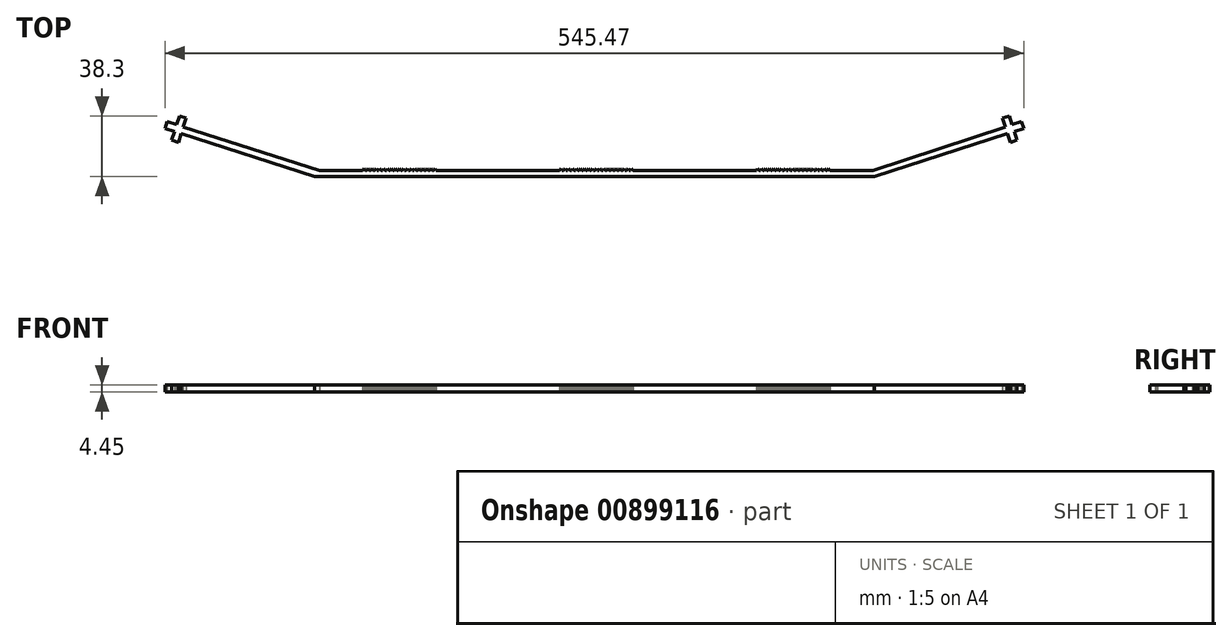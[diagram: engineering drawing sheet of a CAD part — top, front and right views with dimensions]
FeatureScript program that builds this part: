
annotation { "Feature Type Name" : "Feature", "Feature Type Description" : "" }
export const myFeature = defineFeature(function(context is Context, id is Id, definition is map)
    precondition{}
    {
        {
            var Q0;
            Q0=qCreatedBy(makeId("Top.planeOp"),FACE);
            var sketch = newSketch(context, id + "F0", { "sketchPlane" : qUnion([Q0])});
            skLineSegment(sketch, "E0", {"start": v(-248.6, 5.73) * mm, "end": v(107, 5.73) * mm});
            skLineSegment(sketch, "E1", {"start": v(-248.6, 5.73) * mm, "end": v(-333.25, 32.88) * mm});
            skLineSegment(sketch, "E2", {"start": v(-333.25, 32.88) * mm, "end": v(-335.04, 27.33) * mm});
            skLineSegment(sketch, "E3", {"start": v(-335.04, 27.33) * mm, "end": v(-339.27, 28.69) * mm});
            skLineSegment(sketch, "E4", {"start": v(-339.27, 28.69) * mm, "end": v(-337.5, 34.24) * mm});
            skLineSegment(sketch, "E5", {"start": v(-337.5, 34.24) * mm, "end": v(-343.54, 36.18) * mm});
            skLineSegment(sketch, "E6", {"start": v(-343.54, 36.18) * mm, "end": v(-342.18, 40.42) * mm});
            skLineSegment(sketch, "E7", {"start": v(-342.18, 40.42) * mm, "end": v(-336.13, 38.48) * mm});
            skLineSegment(sketch, "E8", {"start": v(-336.13, 38.48) * mm, "end": v(-334.35, 44.03) * mm});
            skLineSegment(sketch, "E9", {"start": v(-334.35, 44.03) * mm, "end": v(-330.11, 42.67) * mm});
            skLineSegment(sketch, "E10", {"start": v(-330.11, 42.67) * mm, "end": v(-331.9, 37.12) * mm});
            skLineSegment(sketch, "E11", {"start": v(-331.9, 37.12) * mm, "end": v(-247.24, 9.97) * mm});
            skLineSegment(sketch, "E12", {"start": v(-245.43, 9.39) * mm, "end": v(-217.94, 9.39) * mm});
            skLineSegment(sketch, "E13", {"start": v(-69.57, 10.53) * mm, "end": v(-68.7, 9.39) * mm});
            skLineSegment(sketch, "E14.MirrorCS", {"start": v(-69.57, 10.53) * mm, "end": v(-70.44, 9.39) * mm});
            skLineSegment(sketch, "E15.trimOffspring", {"start": v(-68.7, 9.39) * mm, "end": v(-67.94, 9.39) * mm});
            skPoint(sketch, "E16.start.orphan", {"position": v(-69.57, 3.34) * mm});
            skLineSegment(sketch, "E17.direction1", {"start": v(-68.7, 9.39) * mm, "end": v(-67.94, 9.39) * mm, "construction": true});
            skLineSegment(sketch, "E18.1.0.0", {"start": v(-67.07, 10.53) * mm, "end": v(-66.2, 9.39) * mm});
            skLineSegment(sketch, "E18.1.0.1", {"start": v(-67.07, 10.53) * mm, "end": v(-67.94, 9.39) * mm});
            skLineSegment(sketch, "E18.2.0.0", {"start": v(-64.57, 10.53) * mm, "end": v(-63.7, 9.39) * mm});
            skLineSegment(sketch, "E18.2.0.1", {"start": v(-64.57, 10.53) * mm, "end": v(-65.44, 9.39) * mm});
            skLineSegment(sketch, "E18.3.0.0", {"start": v(-62.07, 10.53) * mm, "end": v(-61.2, 9.39) * mm});
            skLineSegment(sketch, "E18.3.0.1", {"start": v(-62.07, 10.53) * mm, "end": v(-62.94, 9.39) * mm});
            skLineSegment(sketch, "E18.4.0.0", {"start": v(-59.57, 10.53) * mm, "end": v(-58.7, 9.39) * mm});
            skLineSegment(sketch, "E18.4.0.1", {"start": v(-59.57, 10.53) * mm, "end": v(-60.44, 9.39) * mm});
            skLineSegment(sketch, "E18.5.0.0", {"start": v(-57.07, 10.53) * mm, "end": v(-56.2, 9.39) * mm});
            skLineSegment(sketch, "E18.5.0.1", {"start": v(-57.07, 10.53) * mm, "end": v(-57.94, 9.39) * mm});
            skLineSegment(sketch, "E18.6.0.0", {"start": v(-54.57, 10.53) * mm, "end": v(-53.7, 9.39) * mm});
            skLineSegment(sketch, "E18.6.0.1", {"start": v(-54.57, 10.53) * mm, "end": v(-55.44, 9.39) * mm});
            skLineSegment(sketch, "E18.7.0.0", {"start": v(-52.07, 10.53) * mm, "end": v(-51.2, 9.39) * mm});
            skLineSegment(sketch, "E18.7.0.1", {"start": v(-52.07, 10.53) * mm, "end": v(-52.94, 9.39) * mm});
            skLineSegment(sketch, "E18.8.0.0", {"start": v(-49.57, 10.53) * mm, "end": v(-48.7, 9.39) * mm});
            skLineSegment(sketch, "E18.8.0.1", {"start": v(-49.57, 10.53) * mm, "end": v(-50.44, 9.39) * mm});
            skLineSegment(sketch, "E18.9.0.0", {"start": v(-47.07, 10.53) * mm, "end": v(-46.2, 9.39) * mm});
            skLineSegment(sketch, "E18.9.0.1", {"start": v(-47.07, 10.53) * mm, "end": v(-47.94, 9.39) * mm});
            skLineSegment(sketch, "E19.1.0.0", {"start": v(-72.07, 10.53) * mm, "end": v(-72.94, 9.39) * mm});
            skLineSegment(sketch, "E19.1.0.1", {"start": v(-72.07, 10.53) * mm, "end": v(-71.2, 9.39) * mm});
            skLineSegment(sketch, "E19.2.0.0", {"start": v(-74.57, 10.53) * mm, "end": v(-75.44, 9.39) * mm});
            skLineSegment(sketch, "E19.2.0.1", {"start": v(-74.57, 10.53) * mm, "end": v(-73.7, 9.39) * mm});
            skLineSegment(sketch, "E19.3.0.0", {"start": v(-77.07, 10.53) * mm, "end": v(-77.94, 9.39) * mm});
            skLineSegment(sketch, "E19.3.0.1", {"start": v(-77.07, 10.53) * mm, "end": v(-76.2, 9.39) * mm});
            skLineSegment(sketch, "E19.4.0.0", {"start": v(-79.57, 10.53) * mm, "end": v(-80.44, 9.39) * mm});
            skLineSegment(sketch, "E19.4.0.1", {"start": v(-79.57, 10.53) * mm, "end": v(-78.7, 9.39) * mm});
            skLineSegment(sketch, "E19.5.0.0", {"start": v(-82.07, 10.53) * mm, "end": v(-82.94, 9.39) * mm});
            skLineSegment(sketch, "E19.5.0.1", {"start": v(-82.07, 10.53) * mm, "end": v(-81.2, 9.39) * mm});
            skLineSegment(sketch, "E19.6.0.0", {"start": v(-84.57, 10.53) * mm, "end": v(-85.44, 9.39) * mm});
            skLineSegment(sketch, "E19.6.0.1", {"start": v(-84.57, 10.53) * mm, "end": v(-83.7, 9.39) * mm});
            skLineSegment(sketch, "E19.7.0.0", {"start": v(-87.07, 10.53) * mm, "end": v(-87.94, 9.39) * mm});
            skLineSegment(sketch, "E19.7.0.1", {"start": v(-87.07, 10.53) * mm, "end": v(-86.2, 9.39) * mm});
            skLineSegment(sketch, "E19.8.0.0", {"start": v(-89.57, 10.53) * mm, "end": v(-90.44, 9.39) * mm});
            skLineSegment(sketch, "E19.8.0.1", {"start": v(-89.57, 10.53) * mm, "end": v(-88.7, 9.39) * mm});
            skLineSegment(sketch, "E19.9.0.0", {"start": v(-92.07, 10.53) * mm, "end": v(-92.94, 9.39) * mm});
            skLineSegment(sketch, "E19.9.0.1", {"start": v(-92.07, 10.53) * mm, "end": v(-91.2, 9.39) * mm});
            skLineSegment(sketch, "E19.direction1", {"start": v(-70.44, 9.39) * mm, "end": v(-71.2, 9.39) * mm, "construction": true});
            skLineSegment(sketch, "E20.trimOffspring", {"start": v(-91.2, 9.39) * mm, "end": v(-90.44, 9.39) * mm});
            skLineSegment(sketch, "E21.trimOffspring", {"start": v(-88.7, 9.39) * mm, "end": v(-87.94, 9.39) * mm});
            skLineSegment(sketch, "E22.trimOffspring", {"start": v(-86.2, 9.39) * mm, "end": v(-85.44, 9.39) * mm});
            skLineSegment(sketch, "E23.trimOffspring", {"start": v(-81.2, 9.39) * mm, "end": v(-80.44, 9.39) * mm});
            skLineSegment(sketch, "E24.trimOffspring", {"start": v(-83.7, 9.39) * mm, "end": v(-82.94, 9.39) * mm});
            skLineSegment(sketch, "E25.trimOffspring", {"start": v(-78.7, 9.39) * mm, "end": v(-77.94, 9.39) * mm});
            skLineSegment(sketch, "E26.trimOffspring", {"start": v(-76.2, 9.39) * mm, "end": v(-75.44, 9.39) * mm});
            skLineSegment(sketch, "E27.trimOffspring", {"start": v(-73.7, 9.39) * mm, "end": v(-72.94, 9.39) * mm});
            skLineSegment(sketch, "E28.trimOffspring", {"start": v(-71.2, 9.39) * mm, "end": v(-70.44, 9.39) * mm});
            skLineSegment(sketch, "E29.trimOffspring", {"start": v(-66.2, 9.39) * mm, "end": v(-65.44, 9.39) * mm, "construction": true});
            skLineSegment(sketch, "E30.trimOffspring", {"start": v(-66.2, 9.39) * mm, "end": v(-65.44, 9.39) * mm});
            skLineSegment(sketch, "E31.trimOffspring", {"start": v(-63.7, 9.39) * mm, "end": v(-62.94, 9.39) * mm, "construction": true});
            skLineSegment(sketch, "E32.trimOffspring", {"start": v(-63.7, 9.39) * mm, "end": v(-62.94, 9.39) * mm});
            skLineSegment(sketch, "E33.trimOffspring", {"start": v(-61.2, 9.39) * mm, "end": v(-60.44, 9.39) * mm, "construction": true});
            skLineSegment(sketch, "E34.trimOffspring", {"start": v(-58.7, 9.39) * mm, "end": v(-57.94, 9.39) * mm, "construction": true});
            skLineSegment(sketch, "E35.trimOffspring", {"start": v(-58.7, 9.39) * mm, "end": v(-57.94, 9.39) * mm});
            skLineSegment(sketch, "E36", {"start": v(-61.2, 9.39) * mm, "end": v(-60.44, 9.39) * mm});
            skLineSegment(sketch, "E37.trimOffspring", {"start": v(-56.2, 9.39) * mm, "end": v(-55.44, 9.39) * mm, "construction": true});
            skLineSegment(sketch, "E38.trimOffspring", {"start": v(-56.2, 9.39) * mm, "end": v(-55.44, 9.39) * mm});
            skLineSegment(sketch, "E39.trimOffspring", {"start": v(-53.7, 9.39) * mm, "end": v(-52.94, 9.39) * mm, "construction": true});
            skLineSegment(sketch, "E40.trimOffspring", {"start": v(-53.7, 9.39) * mm, "end": v(-52.94, 9.39) * mm});
            skLineSegment(sketch, "E41.trimOffspring", {"start": v(-51.2, 9.39) * mm, "end": v(-50.44, 9.39) * mm, "construction": true});
            skLineSegment(sketch, "E42.trimOffspring", {"start": v(-51.2, 9.39) * mm, "end": v(-50.44, 9.39) * mm});
            skLineSegment(sketch, "E43.trimOffspring", {"start": v(-48.7, 9.39) * mm, "end": v(-47.94, 9.39) * mm, "construction": true});
            skLineSegment(sketch, "E44.trimOffspring", {"start": v(-48.7, 9.39) * mm, "end": v(-47.94, 9.39) * mm});
            skLineSegment(sketch, "E45.trimOffspring", {"start": v(-46.2, 9.39) * mm, "end": v(-43.7, 9.39) * mm, "construction": true});
            skLineSegment(sketch, "E46.trimOffspring", {"start": v(-46.2, 9.39) * mm, "end": v(32.06, 9.39) * mm});
            skLineSegment(sketch, "E47.1.0.0", {"start": v(77.93, 10.53) * mm, "end": v(78.8, 9.39) * mm});
            skLineSegment(sketch, "E47.1.0.1", {"start": v(77.93, 10.53) * mm, "end": v(77.06, 9.39) * mm});
            skLineSegment(sketch, "E47.1.0.2", {"start": v(75.43, 10.53) * mm, "end": v(76.3, 9.39) * mm});
            skLineSegment(sketch, "E47.1.0.3", {"start": v(75.43, 10.53) * mm, "end": v(74.56, 9.39) * mm});
            skLineSegment(sketch, "E47.1.0.4", {"start": v(72.93, 10.53) * mm, "end": v(73.8, 9.39) * mm});
            skLineSegment(sketch, "E47.1.0.5", {"start": v(72.93, 10.53) * mm, "end": v(72.06, 9.39) * mm});
            skLineSegment(sketch, "E47.1.0.6", {"start": v(70.43, 10.53) * mm, "end": v(71.3, 9.39) * mm});
            skLineSegment(sketch, "E47.1.0.7", {"start": v(70.43, 10.53) * mm, "end": v(69.56, 9.39) * mm});
            skLineSegment(sketch, "E47.1.0.8", {"start": v(67.93, 10.53) * mm, "end": v(68.8, 9.39) * mm});
            skLineSegment(sketch, "E47.1.0.9", {"start": v(67.93, 10.53) * mm, "end": v(67.06, 9.39) * mm});
            skLineSegment(sketch, "E47.1.0.10", {"start": v(65.43, 10.53) * mm, "end": v(66.3, 9.39) * mm});
            skLineSegment(sketch, "E47.1.0.11", {"start": v(65.43, 10.53) * mm, "end": v(64.56, 9.39) * mm});
            skLineSegment(sketch, "E47.1.0.12", {"start": v(62.93, 10.53) * mm, "end": v(63.8, 9.39) * mm});
            skLineSegment(sketch, "E47.1.0.13", {"start": v(62.93, 10.53) * mm, "end": v(62.06, 9.39) * mm});
            skLineSegment(sketch, "E47.1.0.14", {"start": v(60.43, 10.53) * mm, "end": v(61.3, 9.39) * mm});
            skLineSegment(sketch, "E47.1.0.15", {"start": v(60.43, 10.53) * mm, "end": v(59.56, 9.39) * mm});
            skLineSegment(sketch, "E47.1.0.16", {"start": v(57.93, 10.53) * mm, "end": v(58.8, 9.39) * mm});
            skLineSegment(sketch, "E47.1.0.17", {"start": v(57.93, 10.53) * mm, "end": v(57.06, 9.39) * mm});
            skLineSegment(sketch, "E47.1.0.18", {"start": v(55.43, 10.53) * mm, "end": v(56.3, 9.39) * mm});
            skLineSegment(sketch, "E47.1.0.19", {"start": v(55.43, 10.53) * mm, "end": v(54.56, 9.39) * mm});
            skLineSegment(sketch, "E47.1.0.20", {"start": v(52.93, 10.53) * mm, "end": v(53.8, 9.39) * mm});
            skLineSegment(sketch, "E47.1.0.21", {"start": v(52.93, 10.53) * mm, "end": v(52.06, 9.39) * mm});
            skLineSegment(sketch, "E47.1.0.22", {"start": v(50.43, 10.53) * mm, "end": v(51.3, 9.39) * mm});
            skLineSegment(sketch, "E47.1.0.23", {"start": v(50.43, 10.53) * mm, "end": v(49.56, 9.39) * mm});
            skLineSegment(sketch, "E47.1.0.24", {"start": v(47.93, 10.53) * mm, "end": v(48.8, 9.39) * mm});
            skLineSegment(sketch, "E47.1.0.25", {"start": v(47.93, 10.53) * mm, "end": v(47.06, 9.39) * mm});
            skLineSegment(sketch, "E47.1.0.26", {"start": v(45.43, 10.53) * mm, "end": v(46.3, 9.39) * mm});
            skLineSegment(sketch, "E47.1.0.27", {"start": v(45.43, 10.53) * mm, "end": v(44.56, 9.39) * mm});
            skLineSegment(sketch, "E47.1.0.28", {"start": v(42.93, 10.53) * mm, "end": v(43.8, 9.39) * mm});
            skLineSegment(sketch, "E47.1.0.29", {"start": v(42.93, 10.53) * mm, "end": v(42.06, 9.39) * mm});
            skLineSegment(sketch, "E47.1.0.30", {"start": v(40.43, 10.53) * mm, "end": v(41.3, 9.39) * mm});
            skLineSegment(sketch, "E47.1.0.31", {"start": v(40.43, 10.53) * mm, "end": v(39.56, 9.39) * mm});
            skLineSegment(sketch, "E47.1.0.32", {"start": v(37.93, 10.53) * mm, "end": v(38.8, 9.39) * mm});
            skLineSegment(sketch, "E47.1.0.33", {"start": v(37.93, 10.53) * mm, "end": v(37.06, 9.39) * mm});
            skLineSegment(sketch, "E47.1.0.34", {"start": v(35.43, 10.53) * mm, "end": v(36.3, 9.39) * mm});
            skLineSegment(sketch, "E47.1.0.35", {"start": v(35.43, 10.53) * mm, "end": v(34.56, 9.39) * mm});
            skLineSegment(sketch, "E47.1.0.36", {"start": v(32.93, 10.53) * mm, "end": v(33.8, 9.39) * mm});
            skLineSegment(sketch, "E47.1.0.37", {"start": v(32.93, 10.53) * mm, "end": v(32.06, 9.39) * mm});
            skLineSegment(sketch, "E48.1.0.0", {"start": v(-172.07, 10.53) * mm, "end": v(-171.2, 9.39) * mm});
            skLineSegment(sketch, "E48.1.0.1", {"start": v(-172.07, 10.53) * mm, "end": v(-172.94, 9.39) * mm});
            skLineSegment(sketch, "E48.1.0.2", {"start": v(-174.57, 10.53) * mm, "end": v(-173.7, 9.39) * mm});
            skLineSegment(sketch, "E48.1.0.3", {"start": v(-174.57, 10.53) * mm, "end": v(-175.44, 9.39) * mm});
            skLineSegment(sketch, "E48.1.0.4", {"start": v(-177.07, 10.53) * mm, "end": v(-176.2, 9.39) * mm});
            skLineSegment(sketch, "E48.1.0.5", {"start": v(-177.07, 10.53) * mm, "end": v(-177.94, 9.39) * mm});
            skLineSegment(sketch, "E48.1.0.6", {"start": v(-179.57, 10.53) * mm, "end": v(-178.7, 9.39) * mm});
            skLineSegment(sketch, "E48.1.0.7", {"start": v(-179.57, 10.53) * mm, "end": v(-180.44, 9.39) * mm});
            skLineSegment(sketch, "E48.1.0.8", {"start": v(-182.07, 10.53) * mm, "end": v(-181.2, 9.39) * mm});
            skLineSegment(sketch, "E48.1.0.9", {"start": v(-182.07, 10.53) * mm, "end": v(-182.94, 9.39) * mm});
            skLineSegment(sketch, "E48.1.0.10", {"start": v(-184.57, 10.53) * mm, "end": v(-183.7, 9.39) * mm});
            skLineSegment(sketch, "E48.1.0.11", {"start": v(-184.57, 10.53) * mm, "end": v(-185.44, 9.39) * mm});
            skLineSegment(sketch, "E48.1.0.12", {"start": v(-187.07, 10.53) * mm, "end": v(-186.2, 9.39) * mm});
            skLineSegment(sketch, "E48.1.0.13", {"start": v(-187.07, 10.53) * mm, "end": v(-187.94, 9.39) * mm});
            skLineSegment(sketch, "E48.1.0.14", {"start": v(-189.57, 10.53) * mm, "end": v(-188.7, 9.39) * mm});
            skLineSegment(sketch, "E48.1.0.15", {"start": v(-189.57, 10.53) * mm, "end": v(-190.44, 9.39) * mm});
            skLineSegment(sketch, "E48.1.0.16", {"start": v(-192.07, 10.53) * mm, "end": v(-191.2, 9.39) * mm});
            skLineSegment(sketch, "E48.1.0.17", {"start": v(-192.07, 10.53) * mm, "end": v(-192.94, 9.39) * mm});
            skLineSegment(sketch, "E48.1.0.18", {"start": v(-194.57, 10.53) * mm, "end": v(-193.7, 9.39) * mm});
            skLineSegment(sketch, "E48.1.0.19", {"start": v(-194.57, 10.53) * mm, "end": v(-195.44, 9.39) * mm});
            skLineSegment(sketch, "E48.1.0.20", {"start": v(-217.07, 10.53) * mm, "end": v(-217.94, 9.39) * mm});
            skLineSegment(sketch, "E48.1.0.21", {"start": v(-217.07, 10.53) * mm, "end": v(-216.2, 9.39) * mm});
            skLineSegment(sketch, "E48.1.0.22", {"start": v(-214.57, 10.53) * mm, "end": v(-215.44, 9.39) * mm});
            skLineSegment(sketch, "E48.1.0.23", {"start": v(-214.57, 10.53) * mm, "end": v(-213.7, 9.39) * mm});
            skLineSegment(sketch, "E48.1.0.24", {"start": v(-212.07, 10.53) * mm, "end": v(-212.94, 9.39) * mm});
            skLineSegment(sketch, "E48.1.0.25", {"start": v(-212.07, 10.53) * mm, "end": v(-211.2, 9.39) * mm});
            skLineSegment(sketch, "E48.1.0.26", {"start": v(-209.57, 10.53) * mm, "end": v(-210.44, 9.39) * mm});
            skLineSegment(sketch, "E48.1.0.27", {"start": v(-209.57, 10.53) * mm, "end": v(-208.7, 9.39) * mm});
            skLineSegment(sketch, "E48.1.0.28", {"start": v(-207.07, 10.53) * mm, "end": v(-207.94, 9.39) * mm});
            skLineSegment(sketch, "E48.1.0.29", {"start": v(-207.07, 10.53) * mm, "end": v(-206.2, 9.39) * mm});
            skLineSegment(sketch, "E48.1.0.30", {"start": v(-204.57, 10.53) * mm, "end": v(-205.44, 9.39) * mm});
            skLineSegment(sketch, "E48.1.0.31", {"start": v(-204.57, 10.53) * mm, "end": v(-203.7, 9.39) * mm});
            skLineSegment(sketch, "E48.1.0.32", {"start": v(-202.07, 10.53) * mm, "end": v(-202.94, 9.39) * mm});
            skLineSegment(sketch, "E48.1.0.33", {"start": v(-202.07, 10.53) * mm, "end": v(-201.2, 9.39) * mm});
            skLineSegment(sketch, "E48.1.0.34", {"start": v(-199.57, 10.53) * mm, "end": v(-200.44, 9.39) * mm});
            skLineSegment(sketch, "E48.1.0.35", {"start": v(-199.57, 10.53) * mm, "end": v(-198.7, 9.39) * mm});
            skLineSegment(sketch, "E48.1.0.36", {"start": v(-197.07, 10.53) * mm, "end": v(-197.94, 9.39) * mm});
            skLineSegment(sketch, "E48.1.0.37", {"start": v(-197.07, 10.53) * mm, "end": v(-196.2, 9.39) * mm});
            skLineSegment(sketch, "E48.direction1", {"start": v(-46.2, 9.39) * mm, "end": v(-171.2, 9.39) * mm, "construction": true});
            skLineSegment(sketch, "E49.trimOffspring", {"start": v(-216.2, 9.39) * mm, "end": v(-215.44, 9.39) * mm});
            skLineSegment(sketch, "E50.trimOffspring", {"start": v(-213.7, 9.39) * mm, "end": v(-212.94, 9.39) * mm});
            skLineSegment(sketch, "E51.trimOffspring", {"start": v(-211.2, 9.39) * mm, "end": v(-210.44, 9.39) * mm});
            skLineSegment(sketch, "E52.trimOffspring", {"start": v(-208.7, 9.39) * mm, "end": v(-207.94, 9.39) * mm});
            skLineSegment(sketch, "E53.trimOffspring", {"start": v(-206.2, 9.39) * mm, "end": v(-205.44, 9.39) * mm});
            skLineSegment(sketch, "E54.trimOffspring", {"start": v(-203.7, 9.39) * mm, "end": v(-202.94, 9.39) * mm});
            skLineSegment(sketch, "E55.trimOffspring", {"start": v(-201.2, 9.39) * mm, "end": v(-200.44, 9.39) * mm});
            skLineSegment(sketch, "E56.trimOffspring", {"start": v(-198.7, 9.39) * mm, "end": v(-197.94, 9.39) * mm});
            skLineSegment(sketch, "E57.trimOffspring", {"start": v(-196.2, 9.39) * mm, "end": v(-195.44, 9.39) * mm});
            skLineSegment(sketch, "E58.trimOffspring", {"start": v(-193.7, 9.39) * mm, "end": v(-192.94, 9.39) * mm});
            skLineSegment(sketch, "E59.trimOffspring", {"start": v(-191.2, 9.39) * mm, "end": v(-190.44, 9.39) * mm});
            skLineSegment(sketch, "E60.trimOffspring", {"start": v(-188.7, 9.39) * mm, "end": v(-187.94, 9.39) * mm});
            skLineSegment(sketch, "E61.trimOffspring", {"start": v(-186.2, 9.39) * mm, "end": v(-185.44, 9.39) * mm});
            skLineSegment(sketch, "E62.trimOffspring", {"start": v(-183.7, 9.39) * mm, "end": v(-182.94, 9.39) * mm});
            skLineSegment(sketch, "E63.trimOffspring", {"start": v(-181.2, 9.39) * mm, "end": v(-180.44, 9.39) * mm});
            skLineSegment(sketch, "E64.trimOffspring", {"start": v(-178.7, 9.39) * mm, "end": v(-177.94, 9.39) * mm});
            skLineSegment(sketch, "E65.trimOffspring", {"start": v(-176.2, 9.39) * mm, "end": v(-175.44, 9.39) * mm});
            skLineSegment(sketch, "E66.trimOffspring", {"start": v(-173.7, 9.39) * mm, "end": v(-172.94, 9.39) * mm});
            skLineSegment(sketch, "E67.trimOffspring", {"start": v(-171.2, 9.39) * mm, "end": v(-92.94, 9.39) * mm});
            skLineSegment(sketch, "E68.trimOffspring", {"start": v(78.8, 9.39) * mm, "end": v(106.29, 9.39) * mm});
            skLineSegment(sketch, "E69.trimOffspring", {"start": v(76.3, 9.39) * mm, "end": v(77.06, 9.39) * mm, "construction": true});
            skLineSegment(sketch, "E70.trimOffspring", {"start": v(76.3, 9.39) * mm, "end": v(77.06, 9.39) * mm});
            skLineSegment(sketch, "E71.trimOffspring", {"start": v(73.8, 9.39) * mm, "end": v(74.56, 9.39) * mm, "construction": true});
            skLineSegment(sketch, "E72.trimOffspring", {"start": v(73.8, 9.39) * mm, "end": v(74.56, 9.39) * mm});
            skLineSegment(sketch, "E73.trimOffspring", {"start": v(71.3, 9.39) * mm, "end": v(72.06, 9.39) * mm, "construction": true});
            skLineSegment(sketch, "E74.trimOffspring", {"start": v(71.3, 9.39) * mm, "end": v(72.06, 9.39) * mm});
            skLineSegment(sketch, "E75.trimOffspring", {"start": v(68.8, 9.39) * mm, "end": v(69.56, 9.39) * mm, "construction": true});
            skLineSegment(sketch, "E76.trimOffspring", {"start": v(68.8, 9.39) * mm, "end": v(69.56, 9.39) * mm});
            skLineSegment(sketch, "E77.trimOffspring", {"start": v(66.3, 9.39) * mm, "end": v(67.06, 9.39) * mm});
            skLineSegment(sketch, "E78.trimOffspring", {"start": v(63.8, 9.39) * mm, "end": v(64.56, 9.39) * mm});
            skLineSegment(sketch, "E79.trimOffspring", {"start": v(61.3, 9.39) * mm, "end": v(62.06, 9.39) * mm});
            skLineSegment(sketch, "E80.trimOffspring", {"start": v(58.8, 9.39) * mm, "end": v(59.56, 9.39) * mm});
            skLineSegment(sketch, "E81.trimOffspring", {"start": v(56.3, 9.39) * mm, "end": v(57.06, 9.39) * mm});
            skLineSegment(sketch, "E82.trimOffspring", {"start": v(53.8, 9.39) * mm, "end": v(54.56, 9.39) * mm});
            skLineSegment(sketch, "E83.trimOffspring", {"start": v(51.3, 9.39) * mm, "end": v(52.06, 9.39) * mm});
            skLineSegment(sketch, "E84.trimOffspring", {"start": v(48.8, 9.39) * mm, "end": v(49.56, 9.39) * mm});
            skLineSegment(sketch, "E85.trimOffspring", {"start": v(33.8, 9.39) * mm, "end": v(34.56, 9.39) * mm});
            skLineSegment(sketch, "E86.trimOffspring", {"start": v(36.3, 9.39) * mm, "end": v(37.06, 9.39) * mm});
            skLineSegment(sketch, "E87.trimOffspring", {"start": v(38.8, 9.39) * mm, "end": v(39.56, 9.39) * mm});
            skLineSegment(sketch, "E88.trimOffspring", {"start": v(41.3, 9.39) * mm, "end": v(42.06, 9.39) * mm});
            skLineSegment(sketch, "E89.trimOffspring", {"start": v(43.8, 9.39) * mm, "end": v(44.56, 9.39) * mm});
            skLineSegment(sketch, "E90.trimOffspring", {"start": v(46.3, 9.39) * mm, "end": v(47.06, 9.39) * mm});
            skLineSegment(sketch, "E91", {"start": v(-247.24, 9.97) * mm, "end": v(-245.43, 9.39) * mm});
            skLineSegment(sketch, "E92.MirrorCS", {"start": v(193.43, 27.33) * mm, "end": v(197.67, 28.69) * mm});
            skLineSegment(sketch, "E93.MirrorCS", {"start": v(192.75, 44.03) * mm, "end": v(188.51, 42.67) * mm});
            skLineSegment(sketch, "E94.MirrorCS", {"start": v(195.89, 34.24) * mm, "end": v(201.93, 36.18) * mm});
            skLineSegment(sketch, "E95.MirrorCS", {"start": v(191.65, 32.88) * mm, "end": v(193.43, 27.33) * mm});
            skLineSegment(sketch, "E96.MirrorCS", {"start": v(197.67, 28.69) * mm, "end": v(195.89, 34.24) * mm});
            skLineSegment(sketch, "E97.MirrorCS", {"start": v(201.93, 36.18) * mm, "end": v(200.58, 40.42) * mm});
            skLineSegment(sketch, "E98.MirrorCS", {"start": v(200.58, 40.42) * mm, "end": v(194.53, 38.48) * mm});
            skLineSegment(sketch, "E99.MirrorCS", {"start": v(194.53, 38.48) * mm, "end": v(192.75, 44.03) * mm});
            skLineSegment(sketch, "E100.MirrorCS", {"start": v(188.51, 42.67) * mm, "end": v(190.3, 37.12) * mm});
            skLineSegment(sketch, "E101.MirrorCS", {"start": v(107, 5.73) * mm, "end": v(191.65, 32.88) * mm});
            skLineSegment(sketch, "E102.MirrorCS", {"start": v(190.3, 37.12) * mm, "end": v(106.29, 9.39) * mm});
            skSolve(sketch);
        }
        {
            var Q0;
            Q0 = qSketchRegion(id + "F0", true);
            extrude(context, id + "F1", {"entities" : qUnion([Q0]), "depth" : 4.45 * mm, "offsetDistance" : 25 * mm});
        }
    });
